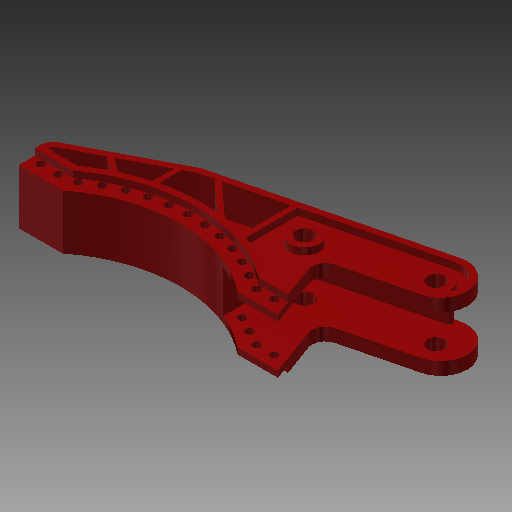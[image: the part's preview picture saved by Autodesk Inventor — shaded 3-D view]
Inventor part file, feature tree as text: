
AUTODESK INVENTOR PART (.ipt)
format: ipt  version: 2018 (Build 220112000, 112)  size: 453,120 bytes
history: native  units: in
note: dims shown in document units (in); Inventor stores cm internally (conversion verified against a paired STEP export)
features: extrude x6, sketch x6, mirror x2, hole x2, plane x1, fillet x1, pattern_linear x1, projected_geometry x1
ambient origin geometry x8: Origin, YZ Plane, XZ Plane, XY Plane, X Axis, Y Axis, Z Axis, Center Point
bodies: Solid1 (feature_tree)
feature tree (20):
  extrude  "Extrusion1"  Depth=0.9958in
  sketch  "Sketch2"  dims[d2=0.4152in d3=0.5696in]
  extrude  "Extrusion2"  Depth=0.5696in
  extrude  "Extrusion3"  Depth=0.25in
  plane  "Work Plane1"
  mirror  "Mirror1"
  sketch  "Sketch3"  dims[d4=0.25in d5=0.5289in]
  extrude  "Extrusion4"  Depth=0.125in
  extrude  "Extrusion5"  Depth=1.4969in
  mirror  "Mirror2"
  extrude  "Extrusion6"  Depth=0.125in
  fillet  "Fillet1"  Radius=0.125in
  hole  "Hole1"  [1 undecoded]
  sketch  "Sketch6"  dims[d10=0.276in d11=0.125in d12=0.125in d13=0.645in d14=0.0in d15=0.3in d16=0.0in d17=0.066in d18=0.0in d21=0.152in d22=0.152in d23=0.559in d24=0.0in d25=0.063in d26=0.0in d27=0.4in d28=0.0in d29=0.165in d30=0.75in d31=0.375in d32=0.25in d33=0.5635in d34=1.0in d35=0.8108in d36=0.284in d37=0.039in d38=0.098in d39=0.078in d40=0.75in d41=0.375in d42=0.25in d43=0.5635in d44=1.0in d45=0.8108in d46=0.098in d47=5.9055in d49=0.039in d50=0.039in]
  hole  "Hole2"  [1 undecoded]
  pattern_linear  "Rectangular Pattern1"  Spacing1=0.066in  [1 undecoded]
  sketch  "Sketch1"  dims[d0=0.8792in d1=0.9958in]
  projected_geometry  "Projected Loop1"
  sketch  "Sketch4"  dims[d6=0.0522in d7=0.125in]
  sketch  "Sketch5"  dims[d8=0.3665in d9=1.4969in]
note: 3 required parameter values undecoded (feature->parameter linkage not recoverable at this tier; creation-order binding heuristic only, values carry confidence <= 0.55)
